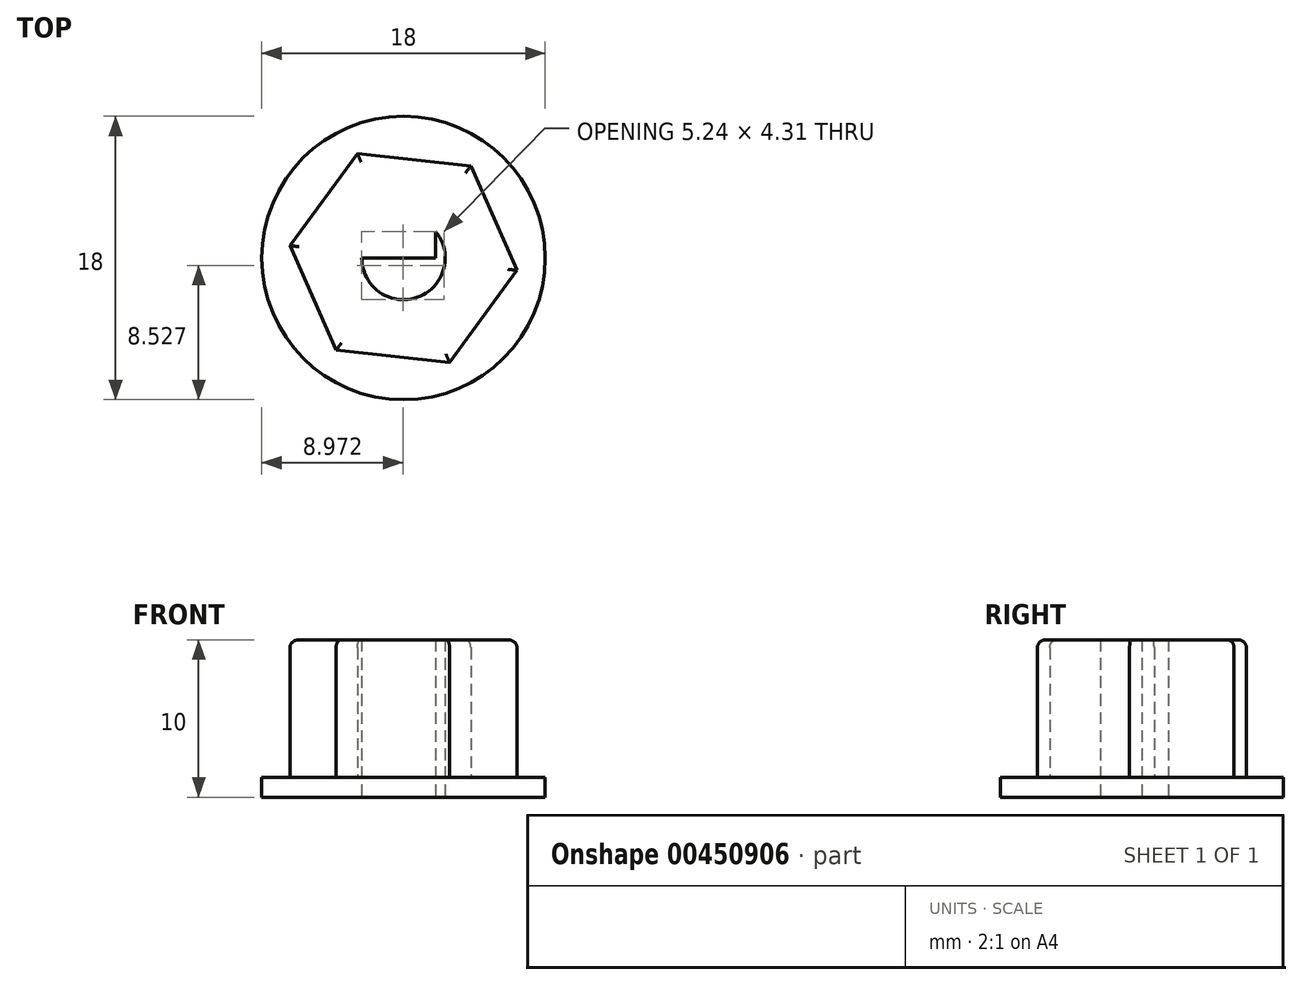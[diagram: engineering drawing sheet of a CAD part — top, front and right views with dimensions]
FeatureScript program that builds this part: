
annotation { "Feature Type Name" : "Feature", "Feature Type Description" : "" }
export const myFeature = defineFeature(function(context is Context, id is Id, definition is map)
    precondition{}
    {
        {
            var Q0;
            Q0=qCreatedBy(makeId("Top.planeOp"),FACE);
            var sketch = newSketch(context, id + "F0", { "sketchPlane" : qUnion([Q0])});
            skCircle(sketch, "E0", {"center": v(0, 0) * mm, "radius": 2.65 * mm});
            skCircle(sketch, "E1.cCircle", {"center": v(0, 0) * mm, "radius": 7.25 * mm, "construction": true});
            skLineSegment(sketch, "E1.0", {"start": v(-4.28, -5.85) * mm, "end": v(-7.2, 0.78) * mm});
            skLineSegment(sketch, "E1.1", {"start": v(-7.2, 0.78) * mm, "end": v(-2.93, 6.63) * mm});
            skLineSegment(sketch, "E1.2", {"start": v(-2.93, 6.63) * mm, "end": v(4.28, 5.85) * mm});
            skLineSegment(sketch, "E1.3", {"start": v(4.28, 5.85) * mm, "end": v(7.2, -0.78) * mm});
            skLineSegment(sketch, "E1.4", {"start": v(7.2, -0.78) * mm, "end": v(2.93, -6.63) * mm});
            skLineSegment(sketch, "E1.5", {"start": v(2.93, -6.63) * mm, "end": v(-4.28, -5.85) * mm});
            skLineSegment(sketch, "E2", {"start": v(-2.65, 0) * mm, "end": v(2.05, 0) * mm});
            skLineSegment(sketch, "E3", {"start": v(2.05, 0) * mm, "end": v(2.05, -1.68) * mm});
            skLineSegment(sketch, "E4", {"start": v(2.05, -1.68) * mm, "end": v(2.05, 1.68) * mm});
            skCircle(sketch, "E5", {"center": v(0, 0) * mm, "radius": 9 * mm});
            skSolve(sketch);
        }
        {
            var Q0;
            Q0=makeQuery(id+"F0.imprint","IMPRINT",FACE,{"disambiguationData":[TD([[makeQuery(id+"F0.imprint","IMPRINT",EDGE,{"derivedFrom":sQuery(id+"F0.wireOp",EDGE,"E1.0")}),-1.0]])]});
            var Q1;
            {var subQ0=sQuery(id+"F0.wireOp",EDGE,"E4");var subQ1=sQuery(id+"F0.wireOp",EDGE,"E0");var subQ2=makeQuery(id+"F0.imprint","INTERSECT",VERTEX,{"disambiguationData":[OD(0.0)],"derivedFrom":[subQ1,subQ0]});Q1=makeQuery(id+"F0.imprint","IMPRINT",FACE,{"disambiguationData":[TD([[makeQuery(id+"F0.imprint","IMPRINT",EDGE,{"disambiguationData":[TD([[subQ2,-1.0]])],"derivedFrom":subQ1}),1.0]])]});}
            extrude(context, id + "F1", {"entities" : qUnion([Q0, Q1]), "depth" : 10 * mm});
        }
        {
            var Q0;
            Q0=makeQuery(id+"F0.imprint","IMPRINT",FACE,{"disambiguationData":[TD([[makeQuery(id+"F0.imprint","IMPRINT",EDGE,{"derivedFrom":sQuery(id+"F0.wireOp",EDGE,"E1.0")}),1.0]])]});
            extrude(context, id + "F2", {"entities" : qUnion([Q0]), "operationType" : NewBodyOperationType.ADD, "depth" : 1.25 * mm});
        }
        {
            var Q0;
            Q0=makeQuery(id+"F1.opExtrude","CAP_EDGE",EDGE,{"disambiguationData":[OSD([sQuery(id+"F0.wireOp",EDGE,"E1.5")])],"isStart":false});
            var Q1;
            Q1=makeQuery(id+"F1.opExtrude","CAP_EDGE",EDGE,{"disambiguationData":[OSD([sQuery(id+"F0.wireOp",EDGE,"E1.4")])],"isStart":false});
            var Q2;
            Q2=makeQuery(id+"F1.opExtrude","CAP_EDGE",EDGE,{"disambiguationData":[OSD([sQuery(id+"F0.wireOp",EDGE,"E1.3")])],"isStart":false});
            var Q3;
            Q3=makeQuery(id+"F1.opExtrude","CAP_EDGE",EDGE,{"disambiguationData":[OSD([sQuery(id+"F0.wireOp",EDGE,"E1.2")])],"isStart":false});
            var Q4;
            Q4=makeQuery(id+"F1.opExtrude","CAP_EDGE",EDGE,{"disambiguationData":[OSD([sQuery(id+"F0.wireOp",EDGE,"E1.1")])],"isStart":false});
            var Q5;
            Q5=makeQuery(id+"F1.opExtrude","CAP_EDGE",EDGE,{"disambiguationData":[OSD([sQuery(id+"F0.wireOp",EDGE,"E1.0")])],"isStart":false});
            fillet(context, id + "F3", {"entities" : qUnion([Q0, Q1, Q2, Q3, Q4, Q5]), "radius" : 0.5 * mm, "tangentPropagation" : true, "allowEdgeOverflow" : false});
        }
    });
